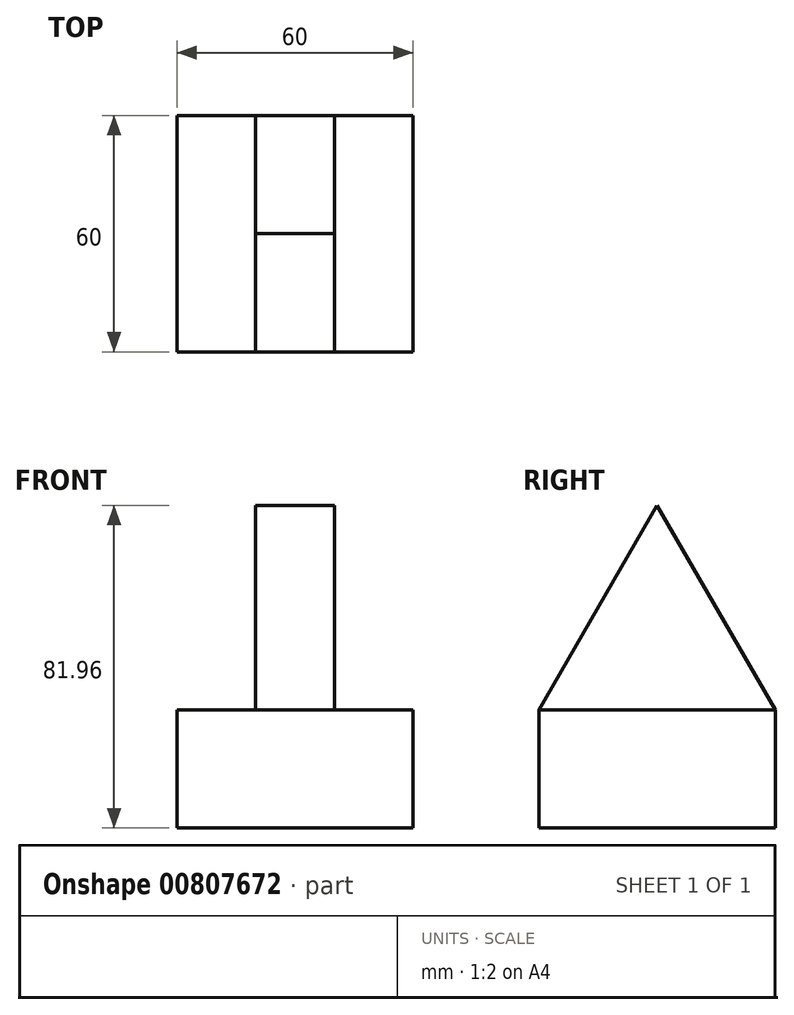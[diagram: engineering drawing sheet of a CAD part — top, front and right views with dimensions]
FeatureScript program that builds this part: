
annotation { "Feature Type Name" : "Feature", "Feature Type Description" : "" }
export const myFeature = defineFeature(function(context is Context, id is Id, definition is map)
    precondition{}
    {
        {
            var Q0;
            Q0=qCreatedBy(makeId("Top.planeOp"),FACE);
            var sketch = newSketch(context, id + "F0", { "sketchPlane" : qUnion([Q0])});
            skLineSegment(sketch, "E0.bottom", {"start": v(-30, 30) * mm, "end": v(30, 30) * mm});
            skLineSegment(sketch, "E0.top", {"start": v(-30, -30) * mm, "end": v(30, -30) * mm});
            skLineSegment(sketch, "E0.left", {"start": v(-30, 30) * mm, "end": v(-30, -30) * mm});
            skLineSegment(sketch, "E0.right", {"start": v(30, 30) * mm, "end": v(30, -30) * mm});
            skPoint(sketch, "E0.middle", {"position": v(0, 0) * mm});
            skSolve(sketch);
        }
        {
            var Q0;
            Q0=makeQuery(id+"F0.imprint","IMPRINT",FACE,{"disambiguationData":[TD([[makeQuery(id+"F0.imprint","IMPRINT",EDGE,{"derivedFrom":sQuery(id+"F0.wireOp",EDGE,"E0.bottom")}),-1.0]])]});
            extrude(context, id + "F1", {"entities" : qUnion([Q0]), "depth" : 30 * mm, "offsetDistance" : 25 * mm});
        }
        {
            var Q0;
            Q0=qCreatedBy(makeId("Right.planeOp"),FACE);
            var sketch = newSketch(context, id + "F2", { "sketchPlane" : qUnion([Q0])});
            skLineSegment(sketch, "E1.0", {"start": v(30, 30) * mm, "end": v(-30, 30) * mm});
            skLineSegment(sketch, "E2", {"start": v(-30, 30) * mm, "end": v(0, 81.96) * mm});
            skLineSegment(sketch, "E3", {"start": v(0, 81.96) * mm, "end": v(30, 30) * mm});
            skSolve(sketch);
        }
        {
            var Q0;
            Q0=makeQuery(id+"F2.imprint","IMPRINT",FACE,{"disambiguationData":[TD([[makeQuery(id+"F2.imprint","IMPRINT",EDGE,{"derivedFrom":sQuery(id+"F2.wireOp",EDGE,"E1.0")}),-1.0]])]});
            extrude(context, id + "F3", {"entities" : qUnion([Q0]), "operationType" : NewBodyOperationType.ADD, "oppositeDirection" : true, "depth" : 10 * mm, "offsetDistance" : 25 * mm, "hasSecondDirection" : true, "secondDirectionOppositeDirection" : false, "secondDirectionDepth" : 10 * mm});
        }
    });
